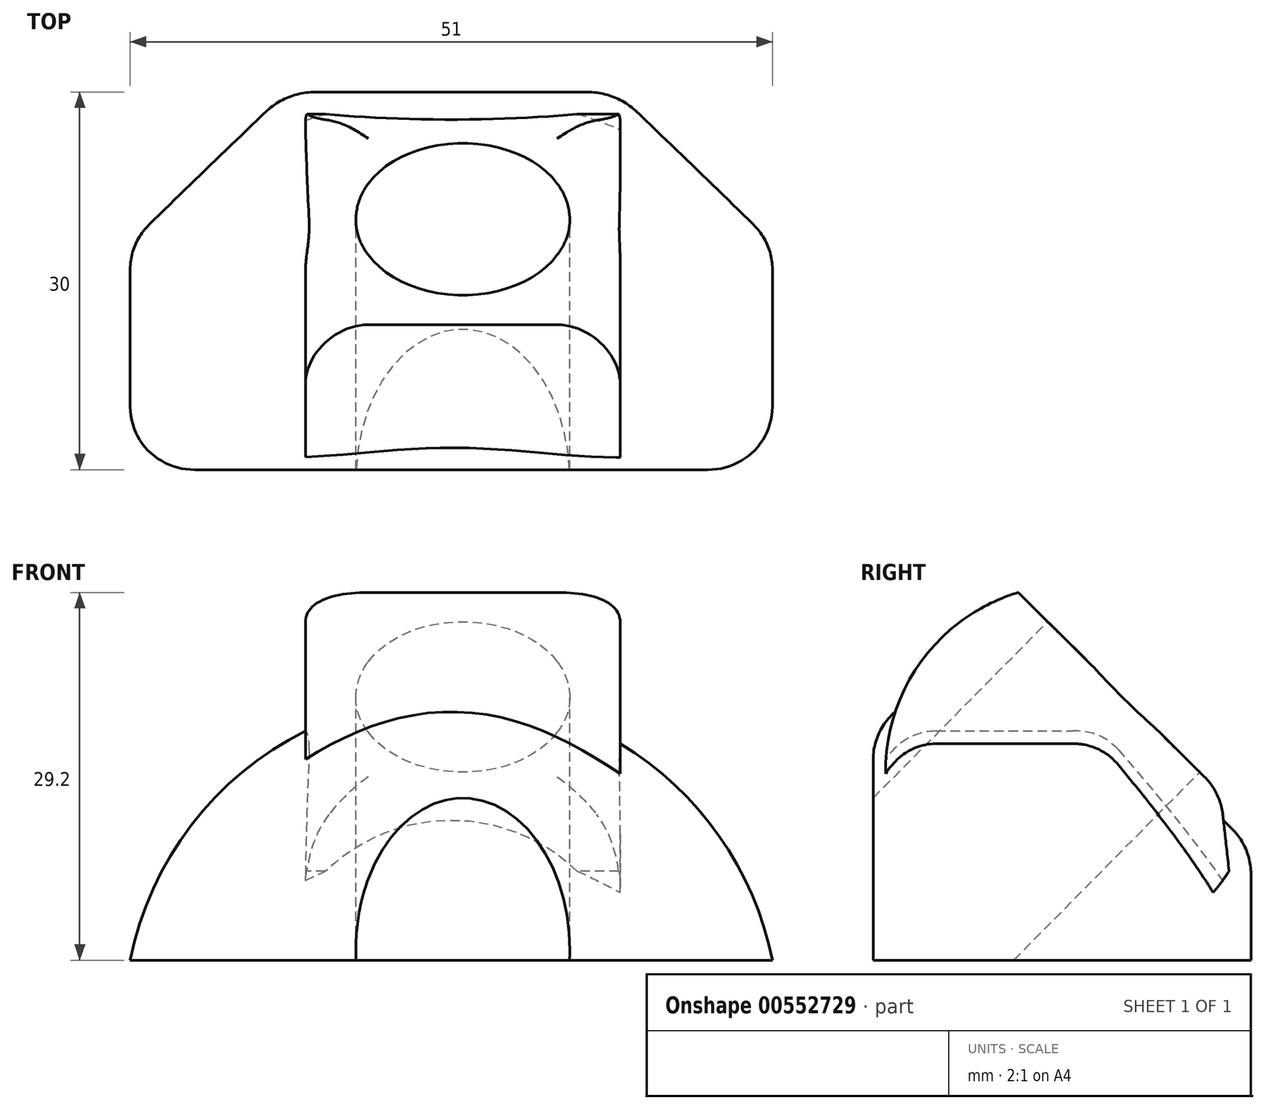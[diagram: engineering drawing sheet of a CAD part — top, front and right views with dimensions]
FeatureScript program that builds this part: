
annotation { "Feature Type Name" : "Feature", "Feature Type Description" : "" }
export const myFeature = defineFeature(function(context is Context, id is Id, definition is map)
    precondition{}
    {
        {
            var Q0;
            Q0=qCreatedBy(makeId("Front.planeOp"),FACE);
            var sketch = newSketch(context, id + "F0", { "sketchPlane" : qUnion([Q0])});
            skLineSegment(sketch, "E0", {"start": v(-26.41, 0) * mm, "end": v(24.59, 0) * mm});
            skArc(sketch, "E1", {"start": v(24.59, 0) * mm, "mid": v(-0.91, 20.93) * mm, "end": v(-26.41, 0) * mm});
            skSolve(sketch);
        }
        {
            var Q0;
            Q0=makeQuery(id+"F0.imprint","IMPRINT",FACE,{"disambiguationData":[TD([[makeQuery(id+"F0.imprint","IMPRINT",EDGE,{"derivedFrom":sQuery(id+"F0.wireOp",EDGE,"E0")}),1.0]])]});
            extrude(context, id + "F1", {"entities" : qUnion([Q0]), "depth" : 30 * mm, "offsetDistance" : 25 * mm});
        }
        {
            var Q0;
            Q0=makeQuery(id+"F1.opExtrude","CAP_EDGE",EDGE,{"disambiguationData":[OSD([sQuery(id+"F0.wireOp",EDGE,"E1")])],"isStart":true});
            chamfer(context, id + "F2", {"entities" : qUnion([Q0]), "width" : 12 * mm});
        }
        {
            var Q0;
            Q0=qCreatedBy(makeId("Right.planeOp"),FACE);
            var sketch = newSketch(context, id + "F3", { "sketchPlane" : qUnion([Q0])});
            skLineSegment(sketch, "E2", {"start": v(0, 10.91) * mm, "end": v(-18.48, 29.2) * mm});
            skArc(sketch, "E3", {"start": v(-18.48, 29.2) * mm, "mid": v(-24.63, 4.51) * mm, "end": v(0, 10.91) * mm});
            skSolve(sketch);
        }
        {
            var Q0;
            Q0=qSketchRegion(id+"F3",true);
            extrude(context, id + "F4", {"entities" : qUnion([Q0]), "operationType" : NewBodyOperationType.ADD, "depth" : 25 * mm, "offsetDistance" : 25 * mm, "symmetric" : true});
        }
        {
            var Q0;
            {var subQ0=sQuery(id+"F3.wireOp",EDGE,"E2");var subQ1=sQuery(id+"F3.wireOp",EDGE,"E3");Q0=makeQuery(id+"F4.boolean.opBoolean","SPLIT",EDGE,{"disambiguationData":[TD([makeQuery(id+"F4.opExtrude","CAP_FACE",FACE,{"disambiguationData":[OSD([subQ0,subQ1])],"isStart":false})])],"derivedFrom":makeQuery(id+"F4.opExtrude","SWEPT_EDGE",EDGE,{"disambiguationData":[OSD([subQ0,subQ1]),TDD([makeQuery(id+"F3.imprint","INTERSECT",VERTEX,{"disambiguationData":[OD(0.0)],"derivedFrom":[subQ0,subQ1]})])]})});}
            var Q1;
            {var subQ0=sQuery(id+"F3.wireOp",EDGE,"E3");var subQ1=sQuery(id+"F3.wireOp",EDGE,"E2");Q1=makeQuery(id+"F4.boolean.opBoolean","SPLIT",EDGE,{"disambiguationData":[TD([makeQuery(id+"F4.opExtrude","CAP_FACE",FACE,{"disambiguationData":[OSD([subQ1,subQ0])],"isStart":true})])],"derivedFrom":makeQuery(id+"F4.opExtrude","SWEPT_EDGE",EDGE,{"disambiguationData":[OSD([subQ1,subQ0]),TDD([makeQuery(id+"F3.imprint","INTERSECT",VERTEX,{"disambiguationData":[OD(0.0)],"derivedFrom":[subQ1,subQ0]})])]})});}
            chamfer(context, id + "F5", {"entities" : qUnion([Q0, Q1]), "width" : 5 * mm, "tangentPropagation" : true});
        }
        {
            var Q0;
            Q0=makeQuery(id+"F4.opExtrude","CAP_EDGE",EDGE,{"disambiguationData":[OSD([sQuery(id+"F3.wireOp",EDGE,"E2")])],"isStart":true});
            var Q1;
            Q1=makeQuery(id+"F4.opExtrude","CAP_EDGE",EDGE,{"disambiguationData":[OSD([sQuery(id+"F3.wireOp",EDGE,"E2")])],"isStart":false});
            var Q2;
            {var subQ0=sQuery(id+"F3.wireOp",EDGE,"E2");var subQ1=makeQuery(id+"F4.opExtrude","SWEPT_FACE",FACE,{"disambiguationData":[OSD([subQ0])]});var subQ2=sQuery(id+"F3.wireOp",EDGE,"E3");Q2=makeQuery(id+"F5.opChamfer","BLEND_EDGE",EDGE,{"blendedFrom":[makeQuery(id+"F4.boolean.opBoolean","SPLIT",EDGE,{"disambiguationData":[TD([makeQuery(id+"F4.opExtrude","CAP_FACE",FACE,{"disambiguationData":[OSD([subQ0,subQ2])],"isStart":false})])],"derivedFrom":makeQuery(id+"F4.opExtrude","SWEPT_EDGE",EDGE,{"disambiguationData":[OSD([subQ0,subQ2]),TDD([makeQuery(id+"F3.imprint","INTERSECT",VERTEX,{"disambiguationData":[OD(0.0)],"derivedFrom":[subQ0,subQ2]})])]})}),subQ1],"blendedInto":[subQ1]});}
            var Q3;
            {var subQ0=sQuery(id+"F3.wireOp",EDGE,"E2");var subQ1=makeQuery(id+"F4.opExtrude","SWEPT_FACE",FACE,{"disambiguationData":[OSD([subQ0])]});var subQ2=sQuery(id+"F3.wireOp",EDGE,"E3");Q3=makeQuery(id+"F5.opChamfer","BLEND_EDGE",EDGE,{"blendedFrom":[makeQuery(id+"F4.boolean.opBoolean","SPLIT",EDGE,{"disambiguationData":[TD([makeQuery(id+"F4.opExtrude","CAP_FACE",FACE,{"disambiguationData":[OSD([subQ0,subQ2])],"isStart":true})])],"derivedFrom":makeQuery(id+"F4.opExtrude","SWEPT_EDGE",EDGE,{"disambiguationData":[OSD([subQ0,subQ2]),TDD([makeQuery(id+"F3.imprint","INTERSECT",VERTEX,{"disambiguationData":[OD(0.0)],"derivedFrom":[subQ0,subQ2]})])]})}),subQ1],"blendedInto":[subQ1]});}
            fillet(context, id + "F6", {"entities" : qUnion([Q0, Q1, Q2, Q3]), "radius" : 5 * mm, "tangentPropagation" : true, "allowEdgeOverflow" : false});
        }
        {
            var Q0;
            Q0=makeQuery(id+"F4.opExtrude","SWEPT_FACE",FACE,{"disambiguationData":[OSD([sQuery(id+"F3.wireOp",EDGE,"E2")])]});
            var sketch = newSketch(context, id + "F7", { "sketchPlane" : qUnion([Q0])});
            skCircle(sketch, "E4", {"center": v(0, -21.89) * mm, "radius": 8.5 * mm});
            skSolve(sketch);
        }
        {
            var Q0;
            Q0=qSketchRegion(id+"F7",true);
            extrude(context, id + "F8", {"entities" : qUnion([Q0]), "operationType" : NewBodyOperationType.REMOVE, "oppositeDirection" : true, "depth" : 30 * mm, "offsetDistance" : 25 * mm});
        }
        {
            var Q0;
            {var subQ0=sQuery(id+"F0.wireOp",EDGE,"E1");var subQ1=makeQuery(id+"F1.opExtrude","SWEPT_FACE",FACE,{"disambiguationData":[OSD([subQ0])]});Q0=makeQuery(id+"F4.boolean.opBoolean","SPLIT",EDGE,{"disambiguationData":[TD([makeQuery(id+"F4.opExtrude","CAP_FACE",FACE,{"disambiguationData":[OSD([sQuery(id+"F3.wireOp",EDGE,"E2"),sQuery(id+"F3.wireOp",EDGE,"E3")])],"isStart":true})])],"derivedFrom":makeQuery(id+"F2.opChamfer","BLEND_EDGE",EDGE,{"blendedFrom":[makeQuery(id+"F1.opExtrude","CAP_EDGE",EDGE,{"disambiguationData":[OSD([subQ0])],"isStart":true}),subQ1],"blendedInto":[subQ1]})});}
            var Q1;
            {var subQ0=sQuery(id+"F0.wireOp",EDGE,"E1");var subQ1=makeQuery(id+"F1.opExtrude","SWEPT_FACE",FACE,{"disambiguationData":[OSD([subQ0])]});Q1=makeQuery(id+"F4.boolean.opBoolean","SPLIT",EDGE,{"disambiguationData":[TD([makeQuery(id+"F4.opExtrude","CAP_FACE",FACE,{"disambiguationData":[OSD([sQuery(id+"F3.wireOp",EDGE,"E2"),sQuery(id+"F3.wireOp",EDGE,"E3")])],"isStart":false})])],"derivedFrom":makeQuery(id+"F2.opChamfer","BLEND_EDGE",EDGE,{"blendedFrom":[makeQuery(id+"F1.opExtrude","CAP_EDGE",EDGE,{"disambiguationData":[OSD([subQ0])],"isStart":true}),subQ1],"blendedInto":[subQ1]})});}
            var Q2;
            Q2=makeQuery(id+"F1.opExtrude","CAP_EDGE",EDGE,{"disambiguationData":[OSD([sQuery(id+"F0.wireOp",EDGE,"E1")])],"isStart":false});
            fillet(context, id + "F9", {"entities" : qUnion([Q0, Q1, Q2]), "radius" : 5 * mm, "tangentPropagation" : true, "allowEdgeOverflow" : false});
        }
        {
            var Q0;
            {var subQ0=sQuery(id+"F0.wireOp",EDGE,"E1");Q0=makeQuery(id+"F2.opChamfer","BLEND_EDGE",EDGE,{"blendedFrom":[makeQuery(id+"F1.opExtrude","CAP_EDGE",EDGE,{"disambiguationData":[OSD([subQ0])],"isStart":true}),makeQuery(id+"F1.opExtrude","CAP_FACE",FACE,{"disambiguationData":[OSD([sQuery(id+"F0.wireOp",EDGE,"E0"),subQ0])],"isStart":true})],"blendedInto":[makeQuery(id+"F1.opExtrude","CAP_FACE",FACE,{"disambiguationData":[OSD([sQuery(id+"F0.wireOp",EDGE,"E0"),subQ0])],"isStart":true})]});}
            fillet(context, id + "F10", {"entities" : qUnion([Q0]), "radius" : 5 * mm, "tangentPropagation" : true, "allowEdgeOverflow" : false});
        }
    });
